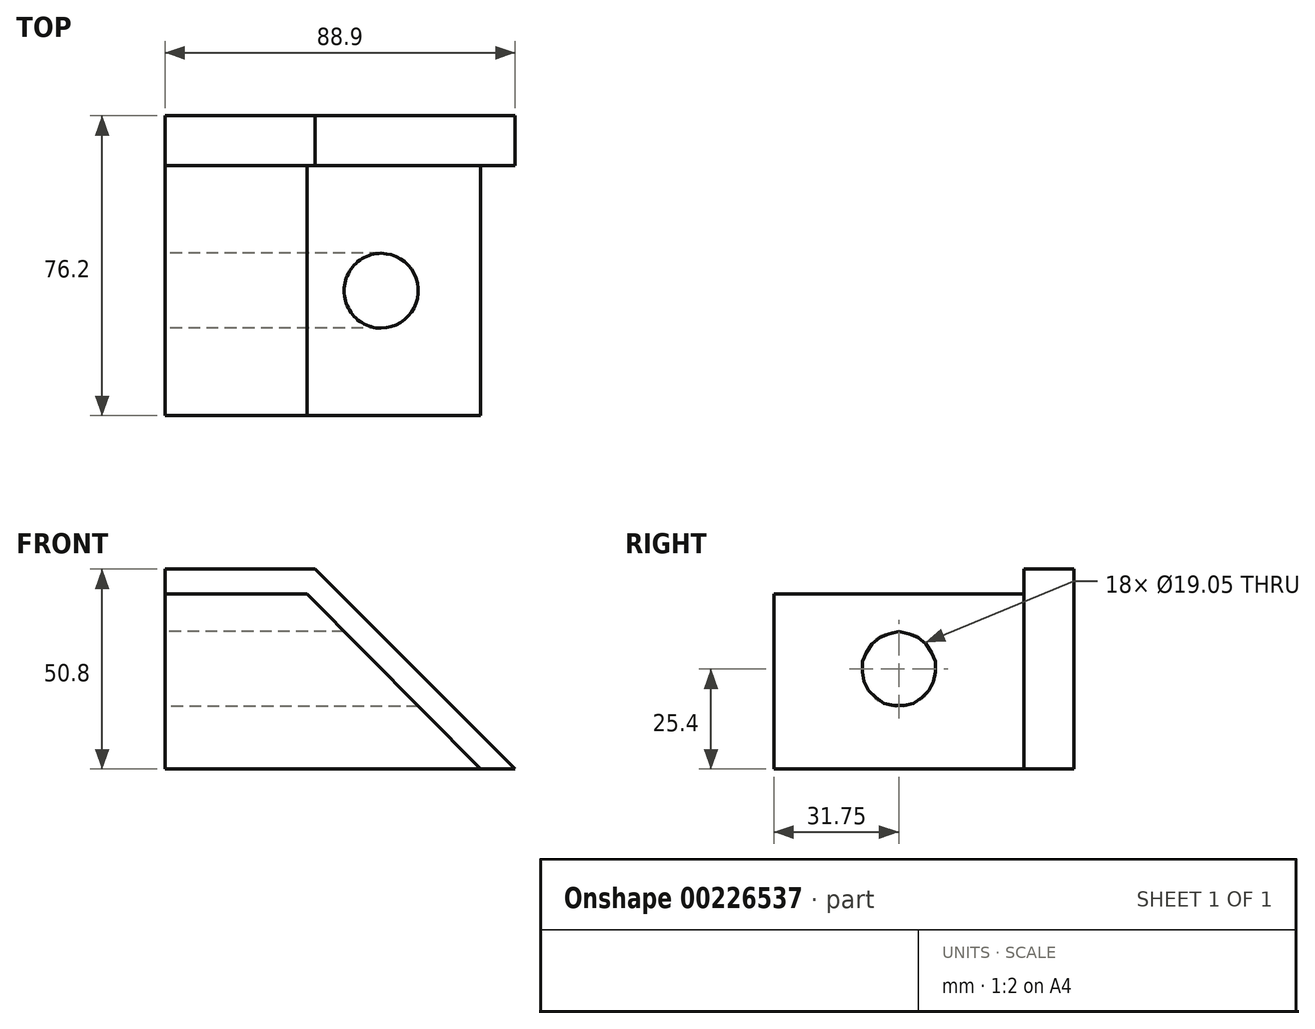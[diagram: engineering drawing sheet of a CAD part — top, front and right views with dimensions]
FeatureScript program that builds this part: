
annotation { "Feature Type Name" : "Feature", "Feature Type Description" : "" }
export const myFeature = defineFeature(function(context is Context, id is Id, definition is map)
    precondition{}
    {
        {
            var Q0;
            Q0=qCreatedBy(makeId("Front.planeOp"),FACE);
            var sketch = newSketch(context, id + "F0", { "sketchPlane" : qUnion([Q0])});
            skLineSegment(sketch, "E0", {"start": v(0, 0) * mm, "end": v(0, 50.8) * mm});
            skLineSegment(sketch, "E1", {"start": v(0, 50.8) * mm, "end": v(38.1, 50.8) * mm});
            skLineSegment(sketch, "E2", {"start": v(38.1, 50.8) * mm, "end": v(88.9, 0) * mm});
            skLineSegment(sketch, "E3", {"start": v(88.9, 0) * mm, "end": v(0, 0) * mm});
            skSolve(sketch);
        }
        {
            var Q0;
            Q0 = qSketchRegion(id + "F0", true);
            extrude(context, id + "F1", {"entities" : qUnion([Q0]), "depth" : 76.2 * mm});
        }
        {
            var Q0;
            Q0=makeQuery(id+"F1.opExtrude","CAP_FACE",FACE,{"disambiguationData":[OSD([sQuery(id+"F0.wireOp",EDGE,"E0"),sQuery(id+"F0.wireOp",EDGE,"E1"),sQuery(id+"F0.wireOp",EDGE,"E2"),sQuery(id+"F0.wireOp",EDGE,"E3")])],"isStart":false});
            var sketch = newSketch(context, id + "F2", { "sketchPlane" : qUnion([Q0])});
            skLineSegment(sketch, "E4", {"start": v(0, 44.45) * mm, "end": v(36.04, 44.45) * mm});
            skLineSegment(sketch, "E5", {"start": v(36.04, 44.45) * mm, "end": v(80.1, 0) * mm});
            skSolve(sketch);
        }
        {
            var Q0;
            Q0 = qSketchRegion(id + "F2", true);
            var Q1;
            {var subQ3=sQuery(id+"F2.wireOp",EDGE,"E4");Q1=makeQuery(id+"F2.imprint","IMPRINT",FACE,{"disambiguationData":[TD([[makeQuery(id+"F2.imprint","IMPRINT",EDGE,{"derivedFrom":subQ3}),1.0]])]});}
            extrude(context, id + "F3", {"entities" : qUnion([Q0, Q1]), "operationType" : NewBodyOperationType.REMOVE, "oppositeDirection" : true, "depth" : 63.5 * mm});
        }
        {
            var Q0;
            Q0=makeQuery(id+"F1.opExtrude","SWEPT_FACE",FACE,{"disambiguationData":[OSD([sQuery(id+"F0.wireOp",EDGE,"E0")])]});
            var sketch = newSketch(context, id + "F4", { "sketchPlane" : qUnion([Q0])});
            skCircle(sketch, "E6", {"center": v(44.45, 25.4) * mm, "radius": 9.53 * mm});
            skSolve(sketch);
        }
        {
            var Q0;
            Q0 = qSketchRegion(id + "F4", true);
            extrude(context, id + "F5", {"entities" : qUnion([Q0]), "operationType" : NewBodyOperationType.REMOVE, "oppositeDirection" : true, "depth" : 101.6 * mm});
        }
    });
